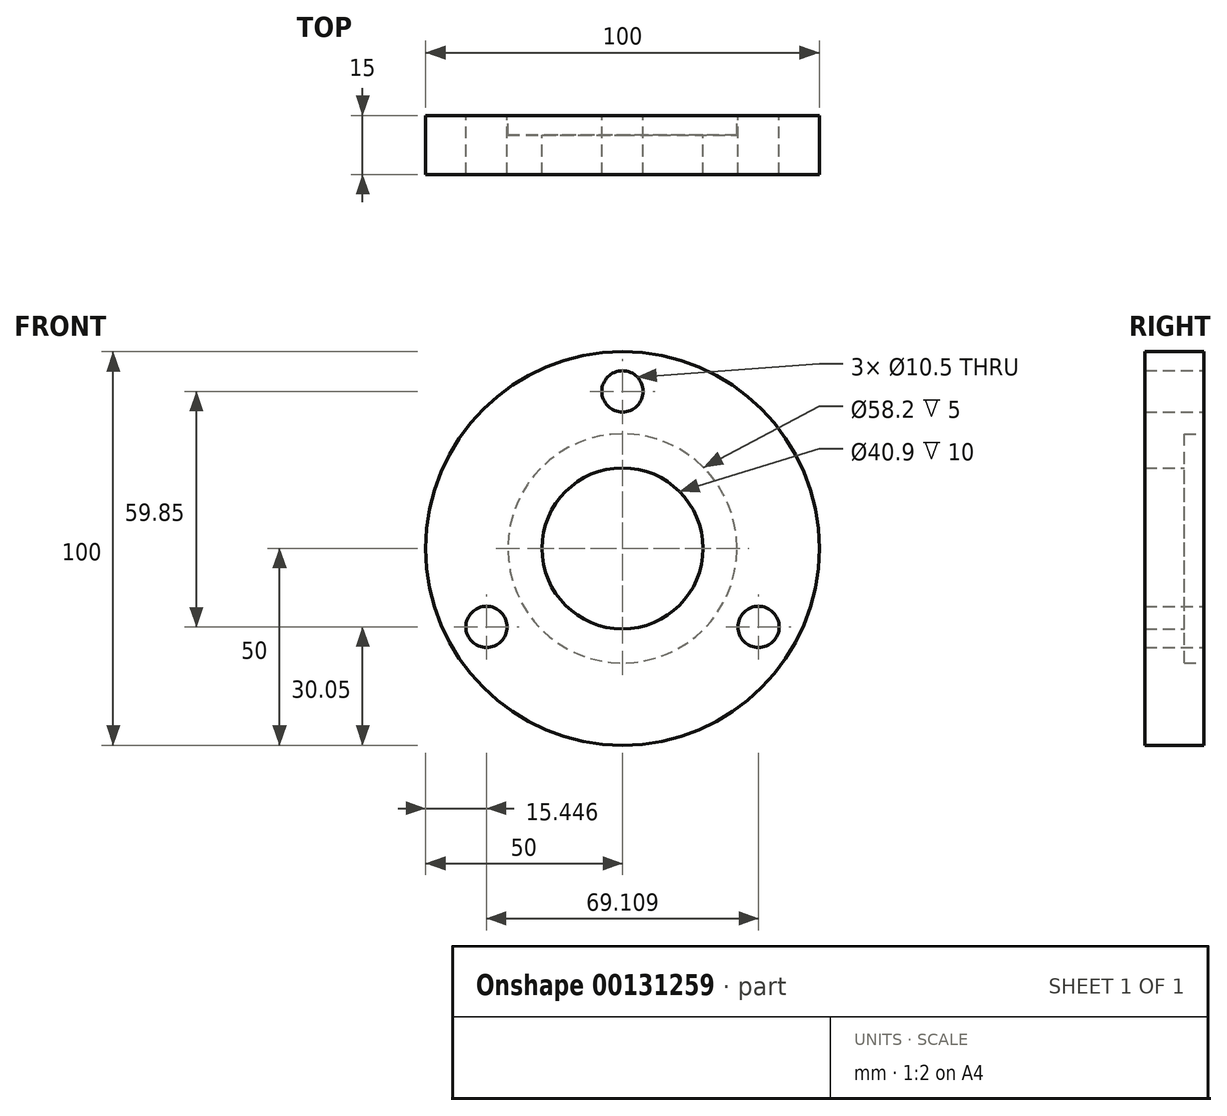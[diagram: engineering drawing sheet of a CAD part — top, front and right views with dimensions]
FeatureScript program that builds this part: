
annotation { "Feature Type Name" : "Feature", "Feature Type Description" : "" }
export const myFeature = defineFeature(function(context is Context, id is Id, definition is map)
    precondition{}
    {
        {
            var Q0;
            Q0=qCreatedBy(makeId("Front.planeOp"),FACE);
            var sketch = newSketch(context, id + "F0", { "sketchPlane" : qUnion([Q0])});
            skCircle(sketch, "E0", {"center": v(0, 0) * mm, "radius": 29.1 * mm});
            skCircle(sketch, "E1", {"center": v(0, 0) * mm, "radius": 39.9 * mm, "construction": true});
            skCircle(sketch, "E2", {"center": v(0, 39.9) * mm, "radius": 5.25 * mm});
            skCircle(sketch, "E3.1.0", {"center": v(-34.55, -19.95) * mm, "radius": 5.25 * mm});
            skCircle(sketch, "E3.2.0", {"center": v(34.55, -19.95) * mm, "radius": 5.25 * mm});
            skCircle(sketch, "E4", {"center": v(0, 0) * mm, "radius": 50 * mm});
            skSolve(sketch);
        }
        {
            var Q0;
            Q0 = qSketchRegion(id + "F0", true);
            extrude(context, id + "F1", {"entities" : qUnion([Q0]), "depth" : 5 * mm});
        }
        {
            var Q0;
            Q0=makeQuery(id+"F1.opExtrude","CAP_FACE",FACE,{"disambiguationData":[OSD([sQuery(id+"F0.wireOp",EDGE,"E0"),sQuery(id+"F0.wireOp",EDGE,"E2"),sQuery(id+"F0.wireOp",EDGE,"E3.1.0"),sQuery(id+"F0.wireOp",EDGE,"E3.2.0"),sQuery(id+"F0.wireOp",EDGE,"E4")])],"isStart":false});
            var sketch = newSketch(context, id + "F2", { "sketchPlane" : qUnion([Q0])});
            skCircle(sketch, "E5", {"center": v(0, 0) * mm, "radius": 20.45 * mm});
            skCircle(sketch, "E6", {"center": v(0, 0) * mm, "radius": 50 * mm});
            skCircle(sketch, "E7", {"center": v(0, 39.9) * mm, "radius": 5.25 * mm});
            skCircle(sketch, "E8.1.0", {"center": v(-34.55, -19.95) * mm, "radius": 5.25 * mm});
            skCircle(sketch, "E8.2.0", {"center": v(34.55, -19.95) * mm, "radius": 5.25 * mm});
            skSolve(sketch);
        }
        {
            var Q0;
            Q0 = qSketchRegion(id + "F2", true);
            extrude(context, id + "F3", {"entities" : qUnion([Q0]), "operationType" : NewBodyOperationType.ADD, "depth" : 10 * mm});
        }
    });
